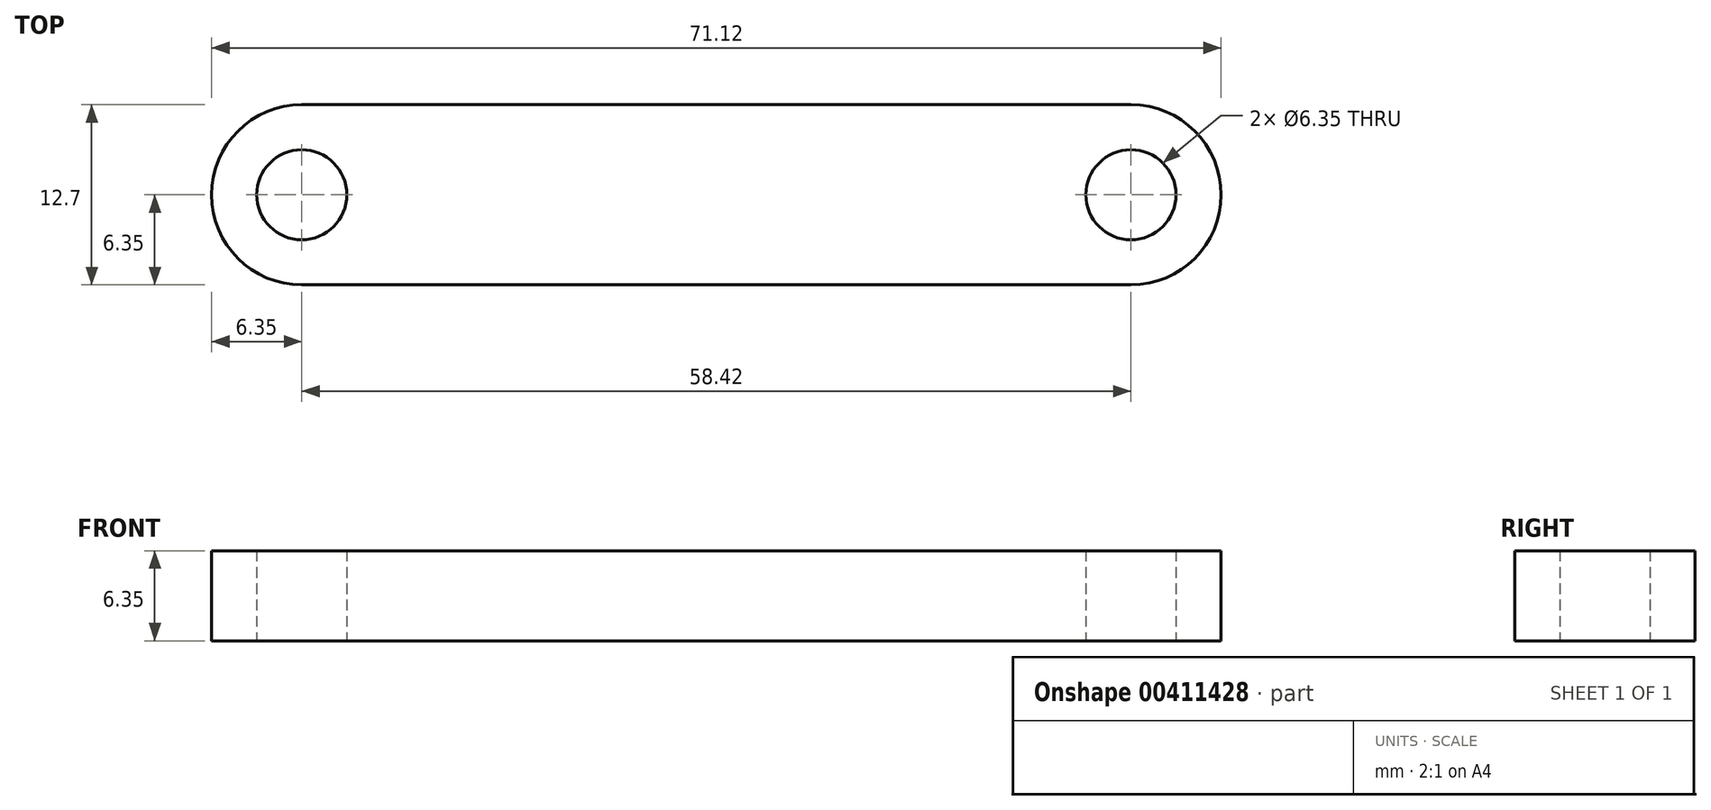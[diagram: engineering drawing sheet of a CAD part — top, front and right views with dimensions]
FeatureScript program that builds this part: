
annotation { "Feature Type Name" : "Feature", "Feature Type Description" : "" }
export const myFeature = defineFeature(function(context is Context, id is Id, definition is map)
    precondition{}
    {
        {
            var Q0;
            Q0=qCreatedBy(makeId("Top.planeOp"),FACE);
            var sketch = newSketch(context, id + "F0", { "sketchPlane" : qUnion([Q0])});
            skLineSegment(sketch, "E0.bottom", {"start": v(-29.2, 6.35) * mm, "end": v(29.21, 6.35) * mm});
            skLineSegment(sketch, "E0.top", {"start": v(-29.21, -6.35) * mm, "end": v(29.21, -6.35) * mm});
            skArc(sketch, "E1", {"start": v(-29.21, 6.35) * mm, "mid": v(-35.56, 0) * mm, "end": v(-29.21, -6.35) * mm});
            skArc(sketch, "E2", {"start": v(29.21, -6.35) * mm, "mid": v(35.56, 0) * mm, "end": v(29.21, 6.35) * mm});
            skCircle(sketch, "E3", {"center": v(-29.21, 0) * mm, "radius": 3.18 * mm});
            skCircle(sketch, "E4", {"center": v(29.21, 0) * mm, "radius": 3.18 * mm});
            skSolve(sketch);
        }
        {
            var Q0;
            Q0=makeQuery(id+"F0.imprint","IMPRINT",FACE,{"disambiguationData":[TD([[makeQuery(id+"F0.imprint","IMPRINT",EDGE,{"derivedFrom":sQuery(id+"F0.wireOp",EDGE,"E0.bottom")}),-1.0]])]});
            extrude(context, id + "F1", {"entities" : qUnion([Q0]), "depth" : 6.35 * mm});
        }
    });
